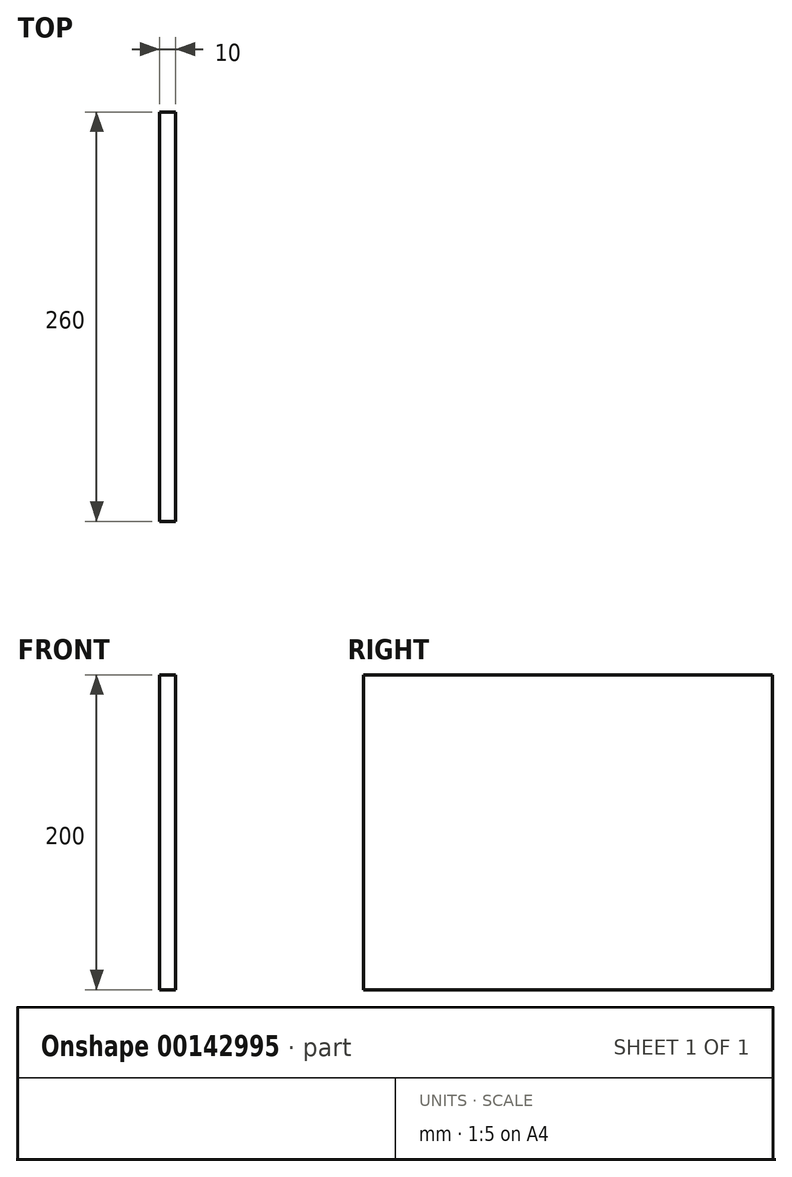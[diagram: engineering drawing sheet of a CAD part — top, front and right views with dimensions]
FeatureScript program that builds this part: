
annotation { "Feature Type Name" : "Feature", "Feature Type Description" : "" }
export const myFeature = defineFeature(function(context is Context, id is Id, definition is map)
    precondition{}
    {
        {
            var Q0;
            Q0=qCreatedBy(makeId("Right.planeOp"),FACE);
            var sketch = newSketch(context, id + "F0", { "sketchPlane" : qUnion([Q0])});
            skLineSegment(sketch, "E0.bottom", {"start": v(0, 0) * mm, "end": v(260, 0) * mm});
            skLineSegment(sketch, "E0.top", {"start": v(0, 200) * mm, "end": v(260, 200) * mm});
            skLineSegment(sketch, "E0.left", {"start": v(0, 0) * mm, "end": v(0, 200) * mm});
            skLineSegment(sketch, "E0.right", {"start": v(260, 0) * mm, "end": v(260, 200) * mm});
            skSolve(sketch);
        }
        {
            var Q0;
            Q0 = qSketchRegion(id + "F0", true);
            extrude(context, id + "F1", {"entities" : qUnion([Q0]), "depth" : 10 * mm, "offsetDistance" : 25 * mm});
        }
    });
